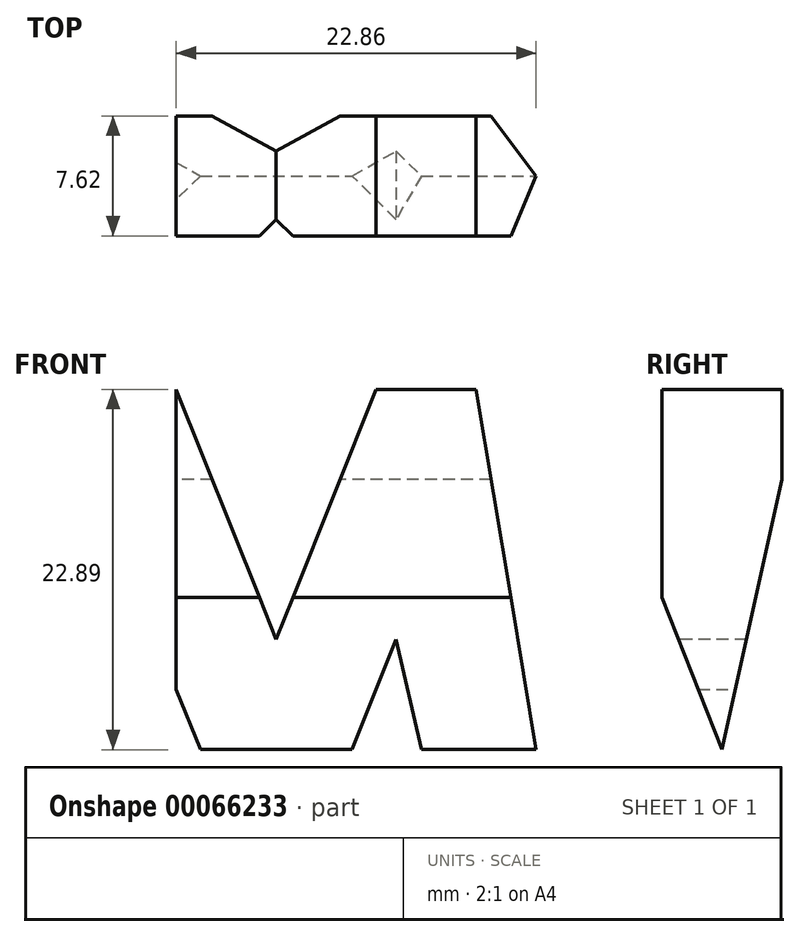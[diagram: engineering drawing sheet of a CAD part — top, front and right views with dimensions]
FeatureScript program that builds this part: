
annotation { "Feature Type Name" : "Feature", "Feature Type Description" : "" }
export const myFeature = defineFeature(function(context is Context, id is Id, definition is map)
    precondition{}
    {
        {
            var Q0;
            Q0=qCreatedBy(makeId("Front.planeOp"),FACE);
            var sketch = newSketch(context, id + "F0", { "sketchPlane" : qUnion([Q0])});
            skLineSegment(sketch, "E0", {"start": v(0, 0) * mm, "end": v(-38.1, 0) * mm});
            skLineSegment(sketch, "E1", {"start": v(-38.1, 0) * mm, "end": v(-38.1, 38.1) * mm});
            skLineSegment(sketch, "E2", {"start": v(-38.1, 38.1) * mm, "end": v(0, 38.1) * mm});
            skLineSegment(sketch, "E3", {"start": v(0, 38.1) * mm, "end": v(0, 0) * mm});
            skSolve(sketch);
        }
        {
            var Q0;
            Q0=qSketchRegion(id+"F0",true);
            var Q1;
            Q1=makeQuery(id+"F0.imprint","IMPRINT",FACE,{"disambiguationData":[TD([[makeQuery(id+"F0.imprint","IMPRINT",EDGE,{"derivedFrom":sQuery(id+"F0.wireOp",EDGE,"E0")}),-1.0]])]});
            extrude(context, id + "F1", {"entities" : qUnion([Q0, Q1]), "depth" : 38.1 * mm});
        }
        {
            var Q0;
            Q0=qCreatedBy(makeId("Front.planeOp"),FACE);
            cPlane(context, id + "F2", {"entities" : qUnion([Q0]), "cplaneType" : CPlaneType.OFFSET, "offset" : 38.1 * mm, "width" : 152.4 * mm, "height" : 152.4 * mm});
        }
        {
            var Q0;
            Q0=qCreatedBy(makeId("Right.planeOp"),FACE);
            cPlane(context, id + "F3", {"entities" : qUnion([Q0]), "cplaneType" : CPlaneType.OFFSET, "offset" : 38.1 * mm, "width" : 152.4 * mm, "height" : 152.4 * mm});
        }
        {
            var Q0;
            Q0=qCreatedBy(makeId("Top.planeOp"),FACE);
            cPlane(context, id + "F4", {"entities" : qUnion([Q0]), "cplaneType" : CPlaneType.OFFSET, "offset" : 38.1 * mm, "width" : 152.4 * mm, "height" : 152.4 * mm});
        }
        {
            var Q0;
            Q0=qCreatedBy(id+"F3.planeOp",FACE);
            var sketch = newSketch(context, id + "F5", { "sketchPlane" : qUnion([Q0])});
            skLineSegment(sketch, "E4", {"start": v(0, 0) * mm, "end": v(0, 38.1) * mm});
            skLineSegment(sketch, "E5", {"start": v(0, 38.1) * mm, "end": v(-38.1, 38.1) * mm});
            skLineSegment(sketch, "E6", {"start": v(-38.1, 38.1) * mm, "end": v(-38.1, 0) * mm});
            skLineSegment(sketch, "E7", {"start": v(-38.1, 0) * mm, "end": v(0, 0) * mm});
            skLineSegment(sketch, "E8", {"start": v(-38.1, 38.1) * mm, "end": v(-31.75, 38.1) * mm});
            skLineSegment(sketch, "E9", {"start": v(-31.75, 38.1) * mm, "end": v(-26.67, 15.39) * mm});
            skLineSegment(sketch, "E10", {"start": v(-26.67, 15.39) * mm, "end": v(-21.59, 28.09) * mm});
            skLineSegment(sketch, "E11", {"start": v(-21.59, 28.09) * mm, "end": v(-16.5, 28.09) * mm});
            skLineSegment(sketch, "E12", {"start": v(-16.5, 28.09) * mm, "end": v(-11.43, 15.21) * mm});
            skLineSegment(sketch, "E13", {"start": v(-11.43, 15.21) * mm, "end": v(-6.35, 38.1) * mm});
            skLineSegment(sketch, "E14", {"start": v(-6.35, 38.1) * mm, "end": v(0, 38.1) * mm});
            skLineSegment(sketch, "E15", {"start": v(0, 38.1) * mm, "end": v(-6.35, 0) * mm});
            skLineSegment(sketch, "E16", {"start": v(-6.35, 0) * mm, "end": v(-12.7, 0) * mm});
            skLineSegment(sketch, "E17", {"start": v(-12.7, 0) * mm, "end": v(-19.05, 15.88) * mm});
            skLineSegment(sketch, "E18", {"start": v(-19.05, 15.88) * mm, "end": v(-25.4, 0) * mm});
            skLineSegment(sketch, "E19", {"start": v(-25.4, 0) * mm, "end": v(-31.75, 0) * mm});
            skLineSegment(sketch, "E20", {"start": v(-31.75, 0) * mm, "end": v(-38.1, 38.1) * mm});
            skSolve(sketch);
        }
        {
            var Q0;
            Q0=makeQuery(id+"F5.imprint","IMPRINT",FACE,{"disambiguationData":[TD([[makeQuery(id+"F5.imprint","IMPRINT",EDGE,{"derivedFrom":sQuery(id+"F5.wireOp",EDGE,"E5")}),1.0]])]});
            var Q1;
            {var subQ0=sQuery(id+"F5.wireOp",EDGE,"E6");Q1=makeQuery(id+"F5.imprint","IMPRINT",FACE,{"disambiguationData":[TD([[makeQuery(id+"F5.imprint","IMPRINT",EDGE,{"derivedFrom":subQ0}),1.0]])]});}
            var Q2;
            {var subQ0=sQuery(id+"F5.wireOp",EDGE,"E17");Q2=makeQuery(id+"F5.imprint","IMPRINT",FACE,{"disambiguationData":[TD([[makeQuery(id+"F5.imprint","IMPRINT",EDGE,{"derivedFrom":subQ0}),1.0]])]});}
            var Q3;
            {var subQ0=sQuery(id+"F5.wireOp",EDGE,"E4");Q3=makeQuery(id+"F5.imprint","IMPRINT",FACE,{"disambiguationData":[TD([[makeQuery(id+"F5.imprint","IMPRINT",EDGE,{"derivedFrom":subQ0}),1.0]])]});}
            extrude(context, id + "F6", {"entities" : qUnion([Q0, Q1, Q2, Q3]), "operationType" : NewBodyOperationType.REMOVE, "oppositeDirection" : true, "depth" : 76.2 * mm});
        }
        {
            var Q0;
            Q0=qCreatedBy(id+"F2.planeOp",FACE);
            var sketch = newSketch(context, id + "F7", { "sketchPlane" : qUnion([Q0])});
            skLineSegment(sketch, "E21", {"start": v(0, 0) * mm, "end": v(0, 38.1) * mm});
            skLineSegment(sketch, "E22", {"start": v(0, 38.1) * mm, "end": v(-38.1, 38.1) * mm});
            skLineSegment(sketch, "E23", {"start": v(-38.1, 38.1) * mm, "end": v(-38.1, 0) * mm});
            skLineSegment(sketch, "E24", {"start": v(-38.1, 0) * mm, "end": v(0, 0) * mm});
            skLineSegment(sketch, "E25", {"start": v(-38.1, 0) * mm, "end": v(-31.75, 38.1) * mm});
            skLineSegment(sketch, "E26", {"start": v(-31.75, 38.1) * mm, "end": v(-25.4, 38.1) * mm});
            skLineSegment(sketch, "E27", {"start": v(-25.4, 38.1) * mm, "end": v(-19.05, 22.23) * mm});
            skLineSegment(sketch, "E28", {"start": v(-19.05, 22.23) * mm, "end": v(-12.7, 38.1) * mm});
            skLineSegment(sketch, "E29", {"start": v(-12.7, 38.1) * mm, "end": v(-6.35, 38.1) * mm});
            skLineSegment(sketch, "E30", {"start": v(-6.35, 38.1) * mm, "end": v(0, 0) * mm});
            skLineSegment(sketch, "E31", {"start": v(-6.35, 0) * mm, "end": v(-11.43, 22.22) * mm});
            skLineSegment(sketch, "E32", {"start": v(-11.43, 22.22) * mm, "end": v(-16.5, 9.53) * mm});
            skLineSegment(sketch, "E33", {"start": v(-16.5, 9.53) * mm, "end": v(-21.59, 9.53) * mm});
            skLineSegment(sketch, "E34", {"start": v(-21.59, 9.52) * mm, "end": v(-26.67, 22.23) * mm});
            skLineSegment(sketch, "E35", {"start": v(-26.67, 22.23) * mm, "end": v(-31.75, 0) * mm});
            skLineSegment(sketch, "E36", {"start": v(-31.75, 0) * mm, "end": v(-38.1, 0) * mm});
            skSolve(sketch);
        }
        {
            var Q0;
            {var subQ0=sQuery(id+"F7.wireOp",EDGE,"E27");Q0=makeQuery(id+"F7.imprint","IMPRINT",FACE,{"disambiguationData":[TD([[makeQuery(id+"F7.imprint","IMPRINT",EDGE,{"derivedFrom":subQ0}),1.0]])]});}
            var Q1;
            {var subQ0=sQuery(id+"F7.wireOp",EDGE,"E23");Q1=makeQuery(id+"F7.imprint","IMPRINT",FACE,{"disambiguationData":[TD([[makeQuery(id+"F7.imprint","IMPRINT",EDGE,{"derivedFrom":subQ0}),1.0]])]});}
            var Q2;
            {var subQ0=sQuery(id+"F7.wireOp",EDGE,"E31");Q2=makeQuery(id+"F7.imprint","IMPRINT",FACE,{"disambiguationData":[TD([[makeQuery(id+"F7.imprint","IMPRINT",EDGE,{"derivedFrom":subQ0}),1.0]])]});}
            var Q3;
            {var subQ0=sQuery(id+"F7.wireOp",EDGE,"E21");Q3=makeQuery(id+"F7.imprint","IMPRINT",FACE,{"disambiguationData":[TD([[makeQuery(id+"F7.imprint","IMPRINT",EDGE,{"derivedFrom":subQ0}),1.0]])]});}
            extrude(context, id + "F8", {"entities" : qUnion([Q0, Q1, Q2, Q3]), "operationType" : NewBodyOperationType.REMOVE, "oppositeDirection" : true, "depth" : 76.2 * mm});
        }
        {
            var Q0;
            Q0=qCreatedBy(id+"F4.planeOp",FACE);
            var sketch = newSketch(context, id + "F9", { "sketchPlane" : qUnion([Q0])});
            skLineSegment(sketch, "E37", {"start": v(0, 0) * mm, "end": v(-38.1, 0) * mm});
            skLineSegment(sketch, "E38", {"start": v(-38.1, 0) * mm, "end": v(-38.1, -38.1) * mm});
            skLineSegment(sketch, "E39", {"start": v(-38.1, -38.1) * mm, "end": v(0, -38.1) * mm});
            skLineSegment(sketch, "E40", {"start": v(0, -38.1) * mm, "end": v(0, 0) * mm});
            skLineSegment(sketch, "E41", {"start": v(-38.1, -22.86) * mm, "end": v(-12.7, -22.86) * mm});
            skLineSegment(sketch, "E42", {"start": v(-12.7, -22.86) * mm, "end": v(-12.7, -30.48) * mm});
            skLineSegment(sketch, "E43", {"start": v(-12.7, -30.48) * mm, "end": v(-38.1, -30.48) * mm});
            skLineSegment(sketch, "E44", {"start": v(-38.1, -30.48) * mm, "end": v(-38.1, -38.1) * mm});
            skLineSegment(sketch, "E45", {"start": v(0, -38.1) * mm, "end": v(0, -15.24) * mm});
            skLineSegment(sketch, "E46", {"start": v(0, -15.24) * mm, "end": v(-25.4, -15.24) * mm});
            skLineSegment(sketch, "E47", {"start": v(-25.4, -15.24) * mm, "end": v(-25.4, -7.62) * mm});
            skLineSegment(sketch, "E48", {"start": v(-25.4, -7.62) * mm, "end": v(0, -7.62) * mm});
            skLineSegment(sketch, "E49", {"start": v(0, -7.62) * mm, "end": v(0, 0) * mm});
            skSolve(sketch);
        }
        {
            var Q0;
            {var subQ2=sQuery(id+"F9.wireOp",EDGE,"E41");Q0=makeQuery(id+"F9.imprint","IMPRINT",FACE,{"disambiguationData":[TD([[makeQuery(id+"F9.imprint","IMPRINT",EDGE,{"derivedFrom":subQ2}),-1.0]])]});}
            var Q1;
            Q1=makeQuery(id+"F9.imprint","IMPRINT",FACE,{"disambiguationData":[TD([[makeQuery(id+"F9.imprint","IMPRINT",EDGE,{"derivedFrom":sQuery(id+"F9.wireOp",EDGE,"E40")}),1.0]])]});
            extrude(context, id + "F10", {"entities" : qUnion([Q0, Q1]), "operationType" : NewBodyOperationType.REMOVE, "oppositeDirection" : true, "depth" : 76.2 * mm});
        }
    });
